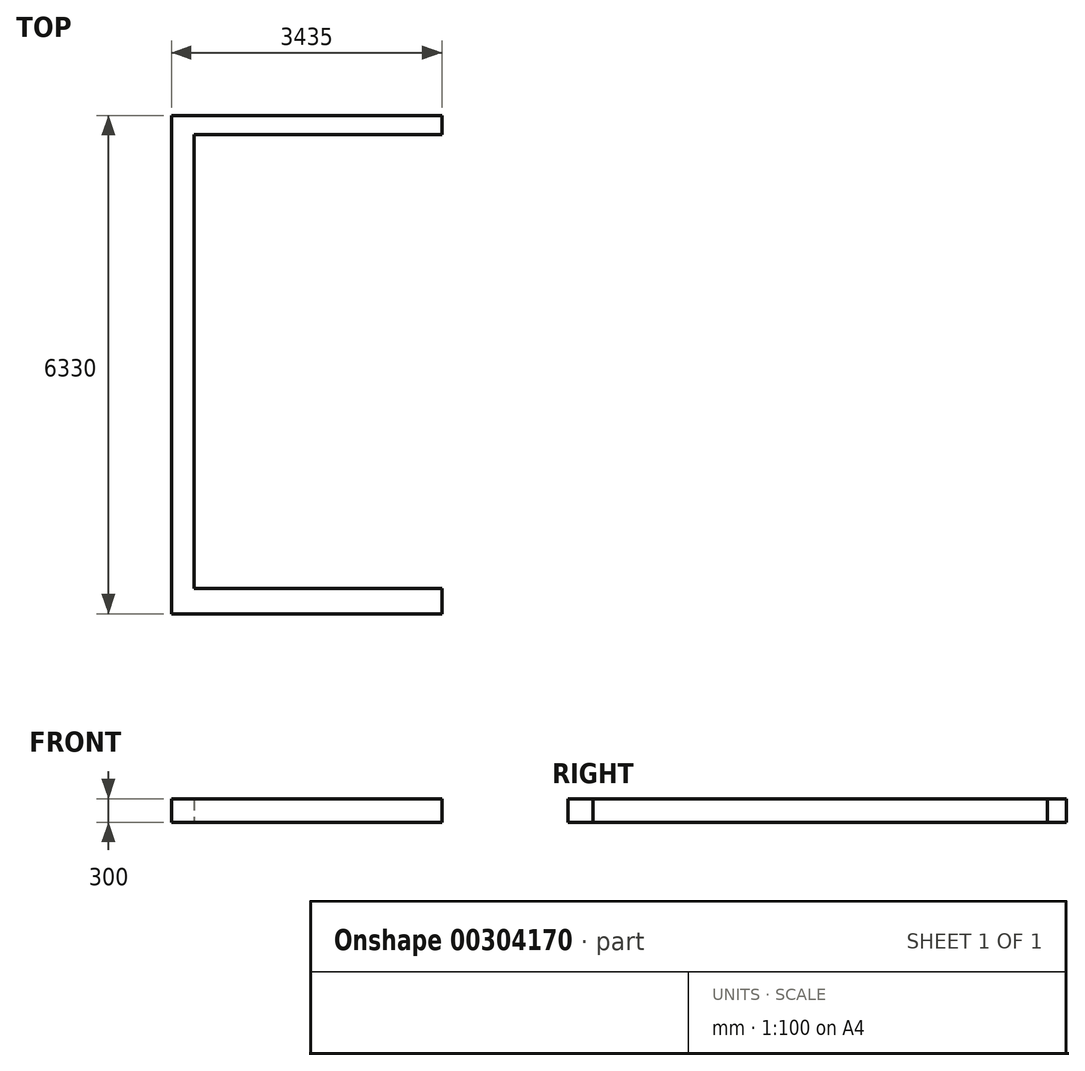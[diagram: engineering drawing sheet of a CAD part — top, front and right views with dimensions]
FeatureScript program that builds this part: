
annotation { "Feature Type Name" : "Feature", "Feature Type Description" : "" }
export const myFeature = defineFeature(function(context is Context, id is Id, definition is map)
    precondition{}
    {
        {
            var Q0;
            Q0=qCreatedBy(makeId("Top.planeOp"),FACE);
            var sketch = newSketch(context, id + "F0", { "sketchPlane" : qUnion([Q0])});
            skLineSegment(sketch, "E0", {"start": v(1551.6, 3017.78) * mm, "end": v(-1883.4, 3017.78) * mm});
            skLineSegment(sketch, "E1", {"start": v(-1883.4, 3017.78) * mm, "end": v(-1883.4, -3312.22) * mm});
            skLineSegment(sketch, "E2", {"start": v(-1883.4, -3312.22) * mm, "end": v(1551.6, -3312.22) * mm});
            skLineSegment(sketch, "E3", {"start": v(1551.6, -3312.22) * mm, "end": v(1551.6, -2992.22) * mm});
            skLineSegment(sketch, "E4", {"start": v(1551.6, -2992.22) * mm, "end": v(-1593.4, -2992.22) * mm});
            skLineSegment(sketch, "E5", {"start": v(-1593.4, -2992.22) * mm, "end": v(-1593.4, 2777.78) * mm});
            skLineSegment(sketch, "E6", {"start": v(-1593.4, 2777.78) * mm, "end": v(1551.6, 2777.78) * mm});
            skLineSegment(sketch, "E7", {"start": v(1551.6, 2777.78) * mm, "end": v(1551.6, 3017.78) * mm});
            skSolve(sketch);
        }
        {
            var Q0;
            Q0=makeQuery(id+"F0.imprint","IMPRINT",FACE,{"disambiguationData":[TD([[makeQuery(id+"F0.imprint","IMPRINT",EDGE,{"derivedFrom":sQuery(id+"F0.wireOp",EDGE,"E0")}),1.0]])]});
            extrude(context, id + "F1", {"entities" : qUnion([Q0]), "depth" : 300 * mm});
        }
    });
